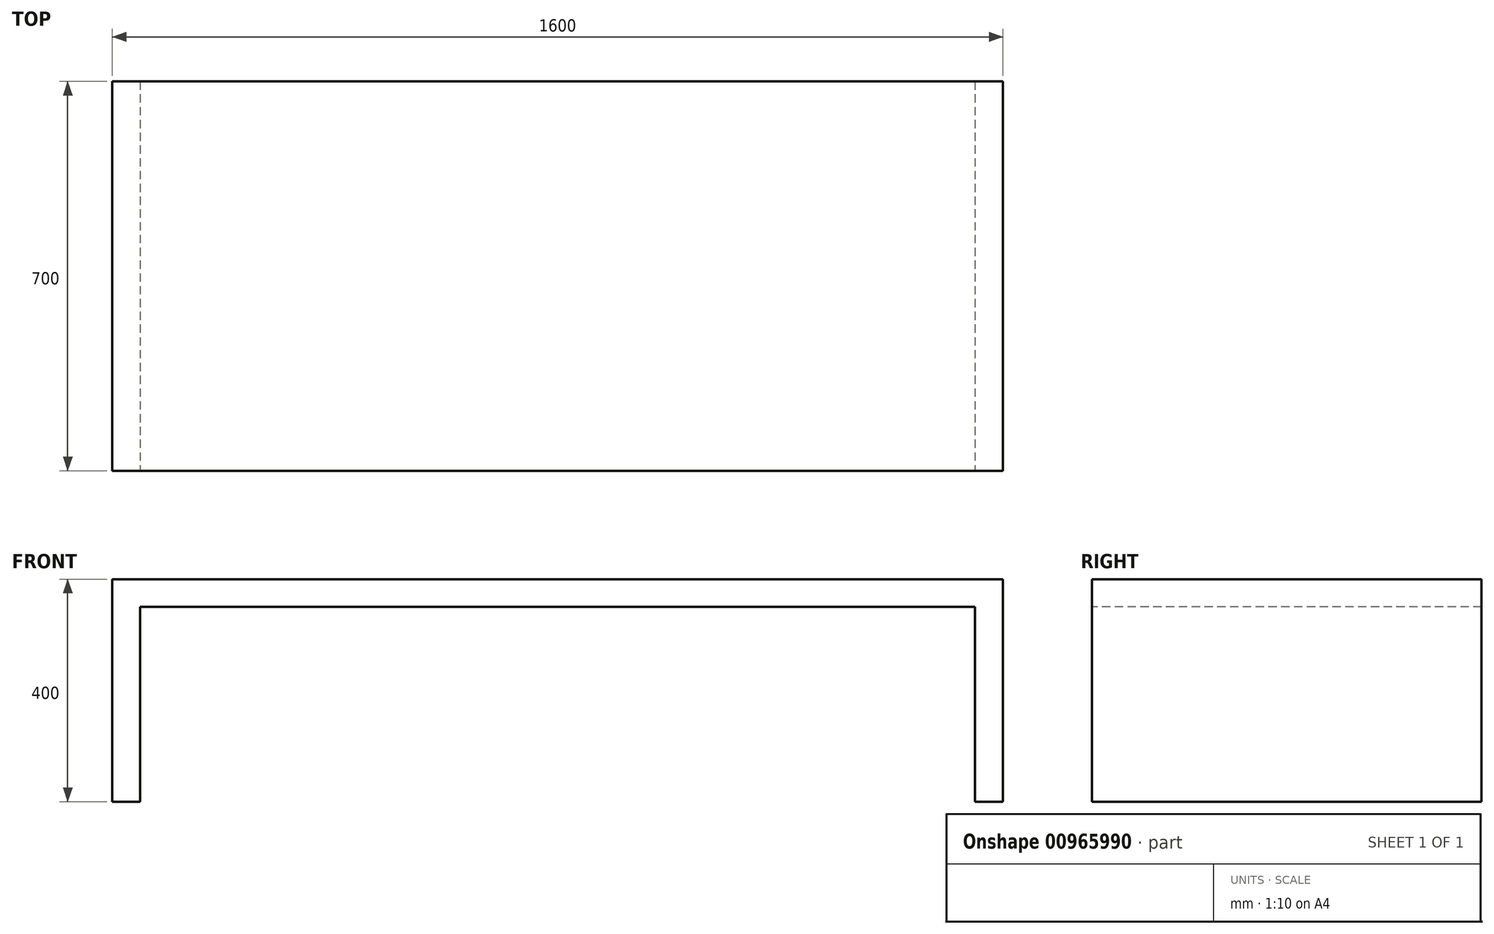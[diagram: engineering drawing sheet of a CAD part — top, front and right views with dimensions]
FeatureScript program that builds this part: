
annotation { "Feature Type Name" : "Feature", "Feature Type Description" : "" }
export const myFeature = defineFeature(function(context is Context, id is Id, definition is map)
    precondition{}
    {
        {
            var Q0;
            Q0=qCreatedBy(makeId("Top.planeOp"),FACE);
            var sketch = newSketch(context, id + "F0", { "sketchPlane" : qUnion([Q0])});
            skLineSegment(sketch, "E0.bottom", {"start": v(-800, 350) * mm, "end": v(800, 350) * mm});
            skLineSegment(sketch, "E0.top", {"start": v(-800, -350) * mm, "end": v(800, -350) * mm});
            skLineSegment(sketch, "E0.left", {"start": v(-800, 350) * mm, "end": v(-800, -350) * mm});
            skLineSegment(sketch, "E0.right", {"start": v(800, 350) * mm, "end": v(800, -350) * mm});
            skLineSegment(sketch, "E1", {"start": v(-800, 350) * mm, "end": v(800, -350) * mm, "construction": true});
            skSolve(sketch);
        }
        {
            var Q0;
            Q0 = qSketchRegion(id + "F0", true);
            extrude(context, id + "F1", {"entities" : qUnion([Q0]), "depth" : 400 * mm, "offsetDistance" : 25 * mm});
        }
        {
            var Q0;
            Q0=makeQuery(id+"F1.opExtrude","CAP_FACE",FACE,{"disambiguationData":[OSD([sQuery(id+"F0.wireOp",EDGE,"E0.bottom"),sQuery(id+"F0.wireOp",EDGE,"E0.top"),sQuery(id+"F0.wireOp",EDGE,"E0.left"),sQuery(id+"F0.wireOp",EDGE,"E0.right")])],"isStart":true});
            var Q1;
            Q1=makeQuery(id+"F1.opExtrude","SWEPT_FACE",FACE,{"disambiguationData":[OSD([sQuery(id+"F0.wireOp",EDGE,"E0.top")])]});
            var Q2;
            Q2=makeQuery(id+"F1.opExtrude","SWEPT_FACE",FACE,{"disambiguationData":[OSD([sQuery(id+"F0.wireOp",EDGE,"E0.bottom")])]});
            shell(context, id + "F2", {"entities" : qUnion([Q0, Q1, Q2]), "thickness" : 50 * mm});
        }
    });
